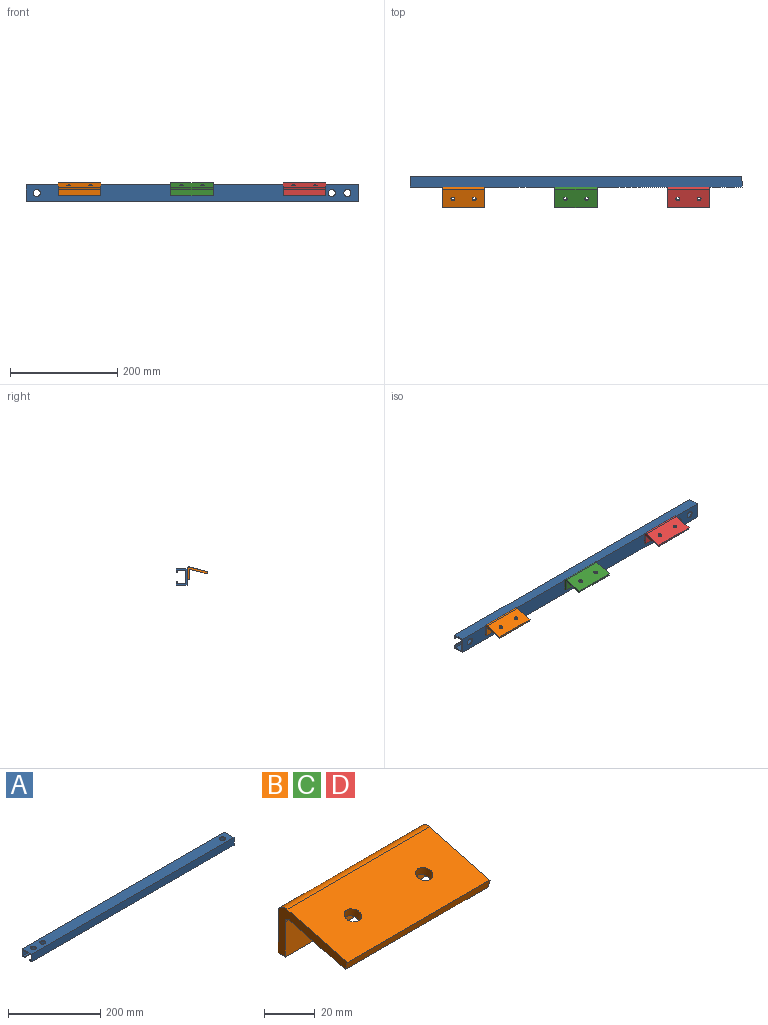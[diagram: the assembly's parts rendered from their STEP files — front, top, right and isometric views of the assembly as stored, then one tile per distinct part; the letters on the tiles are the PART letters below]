
ASSEMBLY  parts=4 mates=3
PART A: 17 faces, bbox 620x30x20 mm
  f0: plane 620x26mm, normal (0,0,-1), area 15721.8mm2, adj f3,f4,f12,f13,f14,f15,f16
  f1: plane 620x30mm, normal (0,0,1), area 18201.8mm2, adj f8,f9,f12,f13,f14,f15,f16
  f2: plane 620x5mm, normal (0,0,1), area 3100mm2, adj f3,f11,f12,f13
  f3: plane 620x16mm, normal (0,1,0), area 9920mm2, adj f0,f2,f12,f13
  f4: plane 620x16mm, normal (0,-1,0), area 9920mm2, adj f0,f5,f12,f13
  f5: plane 620x5mm, normal (0,0,1), area 3100mm2, adj f4,f6,f12,f13
  f6: plane 620x2mm, normal (0,-1,0), area 1240mm2, adj f5,f7,f12,f13
  f7: plane 620x7mm, normal (0,0,-1), area 4340mm2, adj f6,f8,f12,f13
  f8: plane 620x20mm, normal (0,1,0), area 12400mm2, adj f1,f7,f12,f13
  f9: plane 620x20mm, normal (0,-1,0), area 12400mm2, adj f1,f10,f12,f13
  f10: plane 620x7mm, normal (0,0,-1), area 4340mm2, adj f9,f11,f12,f13
  f11: plane 620x2mm, normal (0,1,0), area 1240mm2, adj f2,f10,f12,f13
  f12: plane 30x20mm, normal (-1,0,0), area 152mm2, adj f0,f1,f2,f3,f4,f5,f6,f7
  f13: plane 30x20mm, normal (1,0,0), area 152mm2, adj f0,f1,f2,f3,f4,f5,f6,f7
  f14: cylinder r=6.5mm len=13mm, axis (0,0,1), area 81.7mm2, adj f0,f1
  f15: cylinder r=6.5mm len=13mm, axis (0,0,1), area 81.7mm2, adj f0,f1
  f16: cylinder r=6.5mm len=13mm, axis (0,0,1), area 81.7mm2, adj f0,f1
PART B: 12 faces, bbox 80x38.6x23.8 mm
  f0: plane 80x31.08mm, normal (0,0.26,-0.97), area 2497.5mm2, adj f2,f7,f8,f9,f10,f11
  f1: plane 80x33.6mm, normal (0,-0.26,0.97), area 2706mm2, adj f6,f7,f8,f9,f10,f11
  f2: cylinder r=2mm len=80mm, axis (1,0,0), area 293.2mm2, adj f0,f3,f8,f9
  f3: plane 80x17.18mm, normal (0,-1,0), area 1374.5mm2, adj f2,f4,f8,f9
  f4: plane 80x4mm, normal (0,0,-1), area 320mm2, adj f3,f5,f8,f9
  f5: plane 80x19.79mm, normal (0,1,0), area 1583mm2, adj f4,f6,f8,f9
  f6: cylinder r=4mm len=80mm, axis (1,0,0), area 586.4mm2, adj f1,f5,f8,f9
  f7: plane 80x3.86mm, normal (0,-0.97,-0.26), area 320mm2, adj f0,f1,f8,f9
  f8: plane 38.64x23.79mm, normal (-1,0,0), area 234.5mm2, adj f0,f1,f2,f3,f4,f5,f6,f7
  f9: plane 38.64x23.79mm, normal (1,0,0), area 234.5mm2, adj f0,f1,f2,f3,f4,f5,f6,f7
  f10: cylinder r=3.5mm len=7.8mm, axis (0,-0.26,0.97), area 88mm2, adj f0,f1
  f11: cylinder r=3.5mm len=7.8mm, axis (0,-0.26,0.97), area 88mm2, adj f0,f1
PART C: same geometry as B
PART D: same geometry as B
PLACE A rot(axis=(0,0.71,-0.71),180deg) t=(-368.15,-281.86,-55.17)mm
PLACE B rot(axis=(0.15,0.03,0.99),0deg) t=(-228.15,-301.86,-50.17)mm
PLACE C rot(axis=(0.15,-0.11,0.98),0deg) t=(-18.15,-301.86,-50.17)mm
PLACE D rot(axis=(-0.1,-0.32,0.94),0deg) t=(191.85,-301.86,-50.17)mm
MATE fastened B.f5 <-> A.f1  axis (0,1,0) through (-308.15,-301.86,-75.17)mm
MATE fastened C.f5 <-> A.f1  axis (0,1,0) through (-58.15,-301.86,-75.17)mm
MATE fastened D.f5 <-> A.f1  axis (0,1,0) through (191.85,-301.86,-75.17)mm
